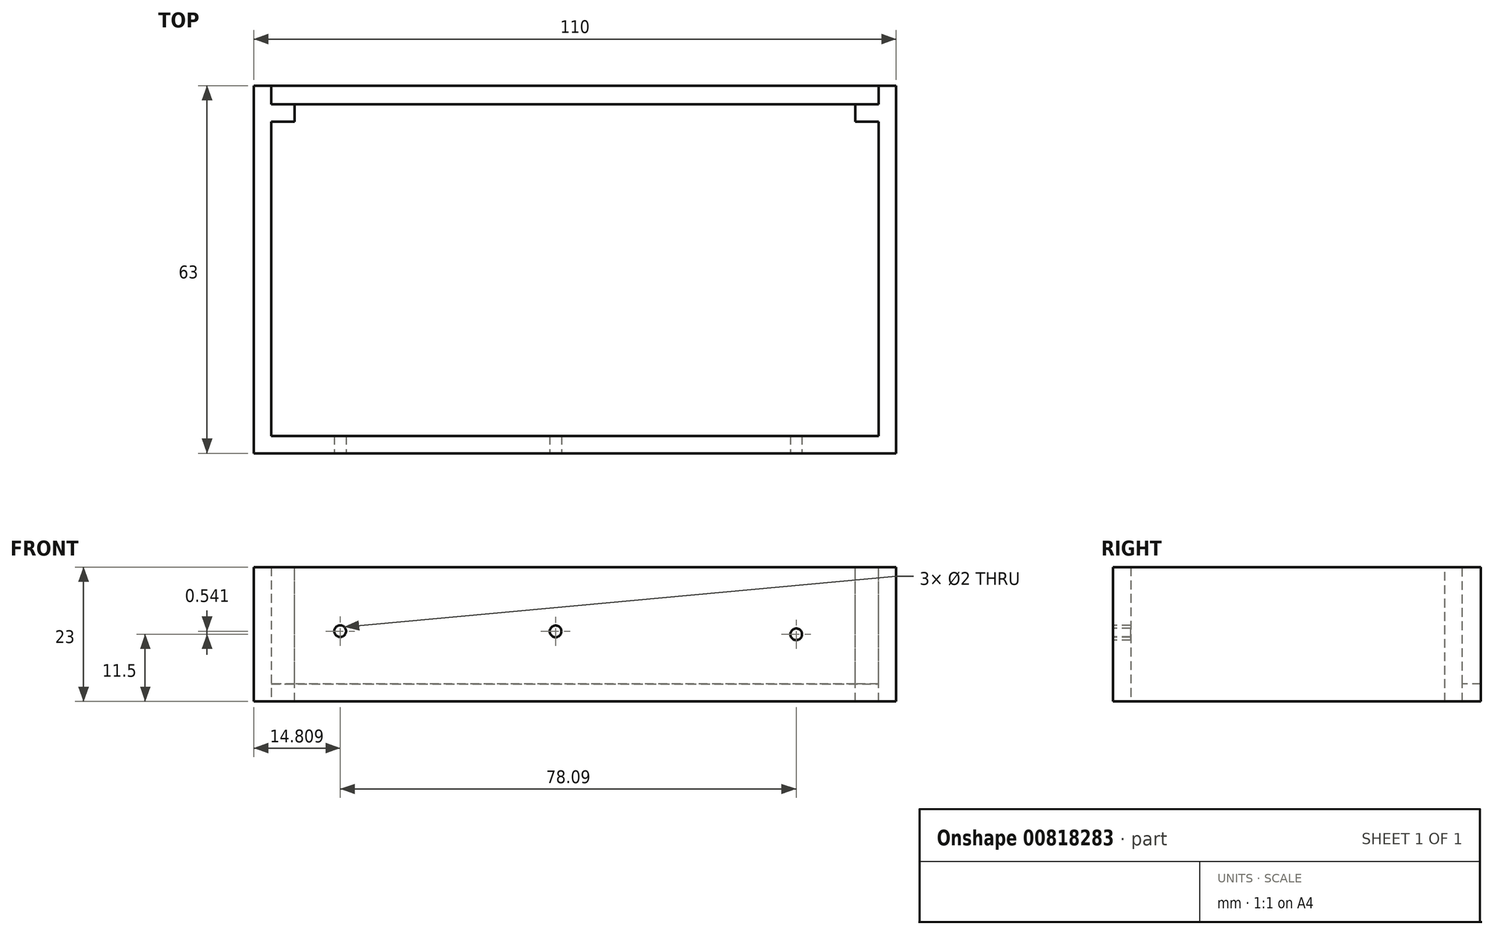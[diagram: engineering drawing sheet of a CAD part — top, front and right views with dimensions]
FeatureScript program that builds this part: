
annotation { "Feature Type Name" : "Feature", "Feature Type Description" : "" }
export const myFeature = defineFeature(function(context is Context, id is Id, definition is map)
    precondition{}
    {
        {
            var Q0;
            Q0=qCreatedBy(makeId("Top.planeOp"),FACE);
            var sketch = newSketch(context, id + "F0", { "sketchPlane" : qUnion([Q0])});
            skLineSegment(sketch, "E0.bottom", {"start": v(-50, 33.03) * mm, "end": v(60, 33.03) * mm});
            skLineSegment(sketch, "E0.top", {"start": v(-50, -32.97) * mm, "end": v(60, -32.97) * mm});
            skLineSegment(sketch, "E0.left", {"start": v(-50, 33.03) * mm, "end": v(-50, -32.97) * mm});
            skLineSegment(sketch, "E0.right", {"start": v(60, 33.03) * mm, "end": v(60, -32.97) * mm});
            skLineSegment(sketch, "E1.left", {"start": v(-50, -32.97) * mm, "end": v(-50, 0.03) * mm});
            skLineSegment(sketch, "E1.right", {"start": v(60, -9.97) * mm, "end": v(60, 0.03) * mm});
            skLineSegment(sketch, "E2.bottom", {"start": v(-50, -32.97) * mm, "end": v(-45, -32.97) * mm});
            skLineSegment(sketch, "E2.top", {"start": v(-60, 33.03) * mm, "end": v(-50, 33.03) * mm});
            skLineSegment(sketch, "E2.left", {"start": v(-50, -32.97) * mm, "end": v(-50, 33.03) * mm});
            skLineSegment(sketch, "E3.bottom", {"start": v(-45, -32.97) * mm, "end": v(-25, -32.97) * mm});
            skLineSegment(sketch, "E3.top", {"start": v(-60, 33.03) * mm, "end": v(-40, 33.03) * mm});
            skLineSegment(sketch, "E4.bottom", {"start": v(-25, -32.97) * mm, "end": v(-5, -32.97) * mm});
            skLineSegment(sketch, "E4.top", {"start": v(-40, 33.03) * mm, "end": v(-20, 33.03) * mm});
            skPoint(sketch, "E5.oppositeSnap0", {"position": v(5, 33.03) * mm});
            skLineSegment(sketch, "E5.bottom", {"start": v(-5, -32.97) * mm, "end": v(15, -32.97) * mm});
            skLineSegment(sketch, "E5.top", {"start": v(-20, 33.03) * mm, "end": v(0, 33.03) * mm});
            skLineSegment(sketch, "E6.bottom", {"start": v(15, -32.97) * mm, "end": v(35, -32.97) * mm});
            skLineSegment(sketch, "E6.top", {"start": v(0, 33.03) * mm, "end": v(20, 33.03) * mm});
            skLineSegment(sketch, "E7.bottom", {"start": v(35, -32.97) * mm, "end": v(55, -32.97) * mm});
            skLineSegment(sketch, "E7.top", {"start": v(20, 33.03) * mm, "end": v(40, 33.03) * mm});
            skLineSegment(sketch, "E8.left", {"start": v(-50, -32.97) * mm, "end": v(-50, -2.97) * mm});
            skLineSegment(sketch, "E8.right", {"start": v(60, -24.97) * mm, "end": v(60, -4.97) * mm});
            skLineSegment(sketch, "E9.left", {"start": v(-50, 33.03) * mm, "end": v(-50, 18.03) * mm});
            skLineSegment(sketch, "E9.right", {"start": v(60, 33.03) * mm, "end": v(60, 18.03) * mm});
            skCircle(sketch, "E10", {"center": v(-15, 1.03) * mm, "radius": 8 * mm});
            skCircle(sketch, "E11", {"center": v(25, -0.47) * mm, "radius": 8 * mm});
            skLineSegment(sketch, "E12.left", {"start": v(-50, -32.97) * mm, "end": v(-50, -17.97) * mm});
            skLineSegment(sketch, "E12.right", {"start": v(60, -32.97) * mm, "end": v(60, -14.97) * mm});
            skLineSegment(sketch, "E13.top", {"start": v(-50, -29.97) * mm, "end": v(60, -29.97) * mm});
            skLineSegment(sketch, "E13.left", {"start": v(-50, -32.97) * mm, "end": v(-50, -29.97) * mm});
            skLineSegment(sketch, "E13.right", {"start": v(60, -32.97) * mm, "end": v(60, -29.97) * mm});
            skSolve(sketch);
        }
        {
            var Q0;
            Q0=makeQuery(id+"F0.imprint","IMPRINT",FACE,{"disambiguationData":[TD([[makeQuery(id+"F0.imprint","IMPRINT",EDGE,{"derivedFrom":sQuery(id+"F0.wireOp",EDGE,"E0.right")}),-1.0]])]});
            extrude(context, id + "F1", {"entities" : qUnion([Q0]), "depth" : 3 * mm, "offsetDistance" : 25 * mm});
        }
        {
            var Q0;
            Q0=makeQuery(id+"F1.opExtrude","CAP_FACE",FACE,{"disambiguationData":[OSD([sQuery(id+"F0.wireOp",EDGE,"E0.right"),sQuery(id+"F0.wireOp",EDGE,"E1.right"),sQuery(id+"F0.wireOp",EDGE,"E2.left"),sQuery(id+"F0.wireOp",EDGE,"E8.left"),sQuery(id+"F0.wireOp",EDGE,"E8.right"),sQuery(id+"F0.wireOp",EDGE,"E0.bottom"),sQuery(id+"F0.wireOp",EDGE,"E9.left"),sQuery(id+"F0.wireOp",EDGE,"E9.right"),sQuery(id+"F0.wireOp",EDGE,"l78r6zbi-zdNL-ogfi-jeJ1-84AOC1EXPDmI"),sQuery(id+"F0.wireOp",EDGE,"7xFXzIXv-dOzj-SHI9-m5NP-5MGqcVb28G0k"),sQuery(id+"F0.wireOp",EDGE,"E10"),sQuery(id+"F0.wireOp",EDGE,"k8Uu2vQ0-tXef-bBox-vRSx-lKBiwxJhI1xb"),sQuery(id+"F0.wireOp",EDGE,"E11"),sQuery(id+"F0.wireOp",EDGE,"5OqNOj1d-C8S8-WuIc-Ppvz-3VOTpNMQOR2k"),sQuery(id+"F0.wireOp",EDGE,"E12.left"),sQuery(id+"F0.wireOp",EDGE,"E12.right"),sQuery(id+"F0.wireOp",EDGE,"HoM0chx2-d7kJ-X9MT-WdqG-gqhH9dmnozYe"),sQuery(id+"F0.wireOp",EDGE,"JgkcrWLJ-2lYI-B5tP-8zwM-9y0SQbQCKJUD"),sQuery(id+"F0.wireOp",EDGE,"uQcqgJcq-6ofs-f9DD-1k3D-WOd607GN4n9v"),sQuery(id+"F0.wireOp",EDGE,"E13.top")])],"isStart":false});
            var sketch = newSketch(context, id + "F2", { "sketchPlane" : qUnion([Q0])});
            skLineSegment(sketch, "E14.bottom", {"start": v(-50, -29.97) * mm, "end": v(60, -29.97) * mm});
            skLineSegment(sketch, "E14.top", {"start": v(-50, -26.97) * mm, "end": v(60, -26.97) * mm});
            skLineSegment(sketch, "E14.left", {"start": v(-50, -29.97) * mm, "end": v(-50, -26.97) * mm});
            skLineSegment(sketch, "E14.right", {"start": v(60, -29.97) * mm, "end": v(60, -26.97) * mm});
            skLineSegment(sketch, "E15.left", {"start": v(-50, 33.03) * mm, "end": v(-50, 30.03) * mm});
            skLineSegment(sketch, "E15.right", {"start": v(60, 33.03) * mm, "end": v(60, 30.03) * mm});
            skLineSegment(sketch, "E16.bottom", {"start": v(-50, 33.03) * mm, "end": v(-47, 33.03) * mm});
            skLineSegment(sketch, "E16.top", {"start": v(-50, -29.97) * mm, "end": v(-47, -29.97) * mm});
            skLineSegment(sketch, "E16.left", {"start": v(-50, 33.03) * mm, "end": v(-50, -29.97) * mm});
            skLineSegment(sketch, "E16.right", {"start": v(-47, 33.03) * mm, "end": v(-47, -29.97) * mm});
            skLineSegment(sketch, "E17.bottom", {"start": v(60, 33.03) * mm, "end": v(57, 33.03) * mm});
            skLineSegment(sketch, "E17.top", {"start": v(60, -29.97) * mm, "end": v(57, -29.97) * mm});
            skLineSegment(sketch, "E17.left", {"start": v(60, 33.03) * mm, "end": v(60, -29.97) * mm});
            skLineSegment(sketch, "E17.right", {"start": v(57, 33.03) * mm, "end": v(57, -29.97) * mm});
            skSolve(sketch);
        }
        {
            var Q0;
            Q0=qSketchRegion(id+"F2",true);
            extrude(context, id + "F3", {"entities" : qUnion([Q0]), "operationType" : NewBodyOperationType.ADD, "depth" : 20 * mm, "offsetDistance" : 25 * mm});
        }
        {
            var Q0;
            Q0=makeQuery(id+"F3.opExtrude","SWEPT_FACE",FACE,{"disambiguationData":[OSD([sQuery(id+"F2.wireOp",EDGE,"E16.right")])]});
            var sketch = newSketch(context, id + "F4", { "sketchPlane" : qUnion([Q0])});
            skLineSegment(sketch, "E18.bottom", {"start": v(33.03, 23) * mm, "end": v(29.83, 23) * mm});
            skLineSegment(sketch, "E18.top", {"start": v(33.03, 3) * mm, "end": v(29.83, 3) * mm});
            skLineSegment(sketch, "E18.left", {"start": v(33.03, 23) * mm, "end": v(33.03, 3) * mm});
            skLineSegment(sketch, "E18.right", {"start": v(29.83, 23) * mm, "end": v(29.83, 3) * mm});
            skLineSegment(sketch, "E19.bottom", {"start": v(29.83, 23) * mm, "end": v(26.83, 23) * mm});
            skLineSegment(sketch, "E19.top", {"start": v(29.83, 3) * mm, "end": v(26.83, 3) * mm});
            skLineSegment(sketch, "E19.right", {"start": v(26.83, 23) * mm, "end": v(26.83, 3) * mm});
            skSolve(sketch);
        }
        {
            var Q0;
            Q0=makeQuery(id+"F4.imprint","IMPRINT",FACE,{"disambiguationData":[TD([[makeQuery(id+"F4.imprint","IMPRINT",EDGE,{"derivedFrom":sQuery(id+"F4.wireOp",EDGE,"E19.bottom")}),1.0]])]});
            extrude(context, id + "F5", {"entities" : qUnion([Q0]), "operationType" : NewBodyOperationType.ADD, "depth" : 104.4 * mm, "offsetDistance" : 25 * mm});
        }
        {
            var Q0;
            Q0=makeQuery(id+"F5.boolean.opBoolean","MERGE",FACE,{"derivedFrom":[makeQuery(id+"F3.opExtrude","CAP_FACE",FACE,{"disambiguationData":[OSD([sQuery(id+"F2.wireOp",EDGE,"E14.bottom"),sQuery(id+"F2.wireOp",EDGE,"E14.top"),sQuery(id+"F2.wireOp",EDGE,"E16.bottom"),sQuery(id+"F2.wireOp",EDGE,"E16.top"),sQuery(id+"F2.wireOp",EDGE,"E16.left"),sQuery(id+"F2.wireOp",EDGE,"E16.right"),sQuery(id+"F2.wireOp",EDGE,"E17.bottom"),sQuery(id+"F2.wireOp",EDGE,"E17.top"),sQuery(id+"F2.wireOp",EDGE,"E17.left"),sQuery(id+"F2.wireOp",EDGE,"E17.right")])],"isStart":false}),makeQuery(id+"F5.opExtrude","SWEPT_FACE",FACE,{"disambiguationData":[OSD([sQuery(id+"F4.wireOp",EDGE,"E19.bottom")])]})]});
            var sketch = newSketch(context, id + "F6", { "sketchPlane" : qUnion([Q0])});
            skLineSegment(sketch, "E20.bottom", {"start": v(-43, 29.83) * mm, "end": v(53, 29.83) * mm});
            skLineSegment(sketch, "E20.top", {"start": v(-43, 26.83) * mm, "end": v(53, 26.83) * mm});
            skLineSegment(sketch, "E20.left", {"start": v(-43, 29.83) * mm, "end": v(-43, 26.83) * mm});
            skLineSegment(sketch, "E20.right", {"start": v(53, 29.83) * mm, "end": v(53, 26.83) * mm});
            skSolve(sketch);
        }
        {
            var Q0;
            Q0=qSketchRegion(id+"F6",true);
            extrude(context, id + "F7", {"entities" : qUnion([Q0]), "operationType" : NewBodyOperationType.REMOVE, "oppositeDirection" : true, "depth" : 40 * mm, "offsetDistance" : 25 * mm});
        }
        {
            var Q0;
            Q0=makeQuery(id+"F3.opExtrude","SWEPT_FACE",FACE,{"disambiguationData":[OSD([sQuery(id+"F2.wireOp",EDGE,"E14.top")])]});
            var sketch = newSketch(context, id + "F8", { "sketchPlane" : qUnion([Q0])});
            skLineSegment(sketch, "E21.bottom", {"start": v(47, 23) * mm, "end": v(-57, 23) * mm});
            skLineSegment(sketch, "E21.left", {"start": v(47, 23) * mm, "end": v(47, 6.99) * mm});
            skLineSegment(sketch, "E21.right", {"start": v(-57, 26.99) * mm, "end": v(-57, 23) * mm});
            skCircle(sketch, "E22", {"center": v(17, 26.99) * mm, "radius": 1.5 * mm});
            skCircle(sketch, "E23", {"center": v(-27, 26.99) * mm, "radius": 1.5 * mm});
            skCircle(sketch, "E24", {"center": v(-20, 26.99) * mm, "radius": 1.5 * mm});
            skSolve(sketch);
        }
        {
            var Q0;
            Q0=makeQuery(id+"F8.imprint","IMPRINT",FACE,{"disambiguationData":[TD([[makeQuery(id+"F8.imprint","IMPRINT",EDGE,{"derivedFrom":sQuery(id+"F8.wireOp",EDGE,"E22")}),1.0]])]});
            var Q1;
            Q1=makeQuery(id+"F8.imprint","IMPRINT",FACE,{"disambiguationData":[TD([[makeQuery(id+"F8.imprint","IMPRINT",EDGE,{"derivedFrom":sQuery(id+"F8.wireOp",EDGE,"E23")}),1.0]])]});
            var Q2;
            Q2=makeQuery(id+"F8.imprint","IMPRINT",FACE,{"disambiguationData":[TD([[makeQuery(id+"F8.imprint","IMPRINT",EDGE,{"derivedFrom":sQuery(id+"F8.wireOp",EDGE,"E24")}),1.0]])]});
            extrude(context, id + "F9", {"entities" : qUnion([Q0, Q1, Q2]), "operationType" : NewBodyOperationType.REMOVE, "oppositeDirection" : true, "depth" : 3 * mm, "offsetDistance" : 25 * mm});
        }
        {
            var Q0;
            {var subQ1=sQuery(id+"F0.wireOp",EDGE,"E0.bottom");var subQ3=sQuery(id+"F0.wireOp",EDGE,"E11");var subQ4=sQuery(id+"F0.wireOp",EDGE,"E10");var subQ5=makeQuery(id+"F1.opExtrude","CAP_FACE",FACE,{"disambiguationData":[OSD([sQuery(id+"F0.wireOp",EDGE,"E0.right"),sQuery(id+"F0.wireOp",EDGE,"E1.right"),sQuery(id+"F0.wireOp",EDGE,"E2.left"),sQuery(id+"F0.wireOp",EDGE,"E8.left"),sQuery(id+"F0.wireOp",EDGE,"E8.right"),subQ1,sQuery(id+"F0.wireOp",EDGE,"E9.left"),sQuery(id+"F0.wireOp",EDGE,"E9.right"),subQ4,subQ3,sQuery(id+"F0.wireOp",EDGE,"E12.left"),sQuery(id+"F0.wireOp",EDGE,"E12.right"),sQuery(id+"F0.wireOp",EDGE,"E13.top")])],"isStart":false});Q0=makeQuery(id+"F7.boolean.opBoolean","MERGE",FACE,{"derivedFrom":[makeQuery(id+"F5.boolean.opBoolean","SPLIT",FACE,{"disambiguationData":[TD([makeQuery(id+"F1.opExtrude","SWEPT_FACE",FACE,{"disambiguationData":[OSD([subQ4])]})])],"derivedFrom":subQ5}),makeQuery(id+"F5.boolean.opBoolean","SPLIT",FACE,{"disambiguationData":[TD([makeQuery(id+"F1.opExtrude","SWEPT_FACE",FACE,{"disambiguationData":[OSD([subQ1])]})])],"derivedFrom":subQ5}),makeQuery(id+"F7.opExtrude","CAP_FACE",FACE,{"disambiguationData":[OSD([sQuery(id+"F6.wireOp",EDGE,"E20.bottom"),sQuery(id+"F6.wireOp",EDGE,"E20.top"),sQuery(id+"F6.wireOp",EDGE,"E20.left"),sQuery(id+"F6.wireOp",EDGE,"E20.right")])],"isStart":false})]});}
            var sketch = newSketch(context, id + "F10", { "sketchPlane" : qUnion([Q0])});
            skSolve(sketch);
        }
        {
            var Q0;
            {var subQ3=sQuery(id+"F0.wireOp",EDGE,"E10");Q0=makeQuery(id+"F10.imprint","IMPRINT",FACE,{"disambiguationData":[TD([[makeQuery(id+"F10.imprint","IMPRINT",EDGE,{"derivedFrom":makeQuery(id+"F1.opExtrude","CAP_EDGE",EDGE,{"disambiguationData":[OSD([subQ3])],"isStart":false})}),-1.0]])]});}
            var sketch = newSketch(context, id + "F11", { "sketchPlane" : qUnion([Q0])});
            skSolve(sketch);
        }
        {
            var Q0;
            Q0=qSketchRegion(id+"F11",true);
            var Q1;
            {var subQ3=sQuery(id+"F0.wireOp",EDGE,"E10");Q1=makeQuery(id+"F10.imprint","IMPRINT",FACE,{"disambiguationData":[TD([[makeQuery(id+"F10.imprint","IMPRINT",EDGE,{"derivedFrom":makeQuery(id+"F1.opExtrude","CAP_EDGE",EDGE,{"disambiguationData":[OSD([subQ3])],"isStart":false})}),-1.0]])]});}
            extrude(context, id + "F12", {"entities" : qUnion([Q0, Q1]), "operationType" : NewBodyOperationType.REMOVE, "oppositeDirection" : true, "depth" : 40 * mm, "offsetDistance" : 25 * mm});
        }
        {
            var Q0;
            Q0=makeQuery(id+"F3.boolean.opBoolean","MERGE",FACE,{"derivedFrom":[makeQuery(id+"F1.opExtrude","SWEPT_FACE",FACE,{"disambiguationData":[OSD([sQuery(id+"F0.wireOp",EDGE,"E13.top")])]}),makeQuery(id+"F3.opExtrude","SWEPT_FACE",FACE,{"disambiguationData":[OSD([sQuery(id+"F2.wireOp",EDGE,"E14.bottom"),sQuery(id+"F2.wireOp",EDGE,"E16.top"),sQuery(id+"F2.wireOp",EDGE,"E17.top")])]})]});
            var sketch = newSketch(context, id + "F13", { "sketchPlane" : qUnion([Q0])});
            skCircle(sketch, "E25", {"center": v(-35.2, 12.04) * mm, "radius": 1 * mm});
            skCircle(sketch, "E26", {"center": v(1.7, 12) * mm, "radius": 1 * mm});
            skCircle(sketch, "E27", {"center": v(42.9, 11.5) * mm, "radius": 1 * mm});
            skSolve(sketch);
        }
        {
            var Q0;
            Q0=qSketchRegion(id+"F13",true);
            extrude(context, id + "F14", {"entities" : qUnion([Q0]), "operationType" : NewBodyOperationType.REMOVE, "oppositeDirection" : true, "depth" : 3 * mm, "offsetDistance" : 25 * mm});
        }
    });
